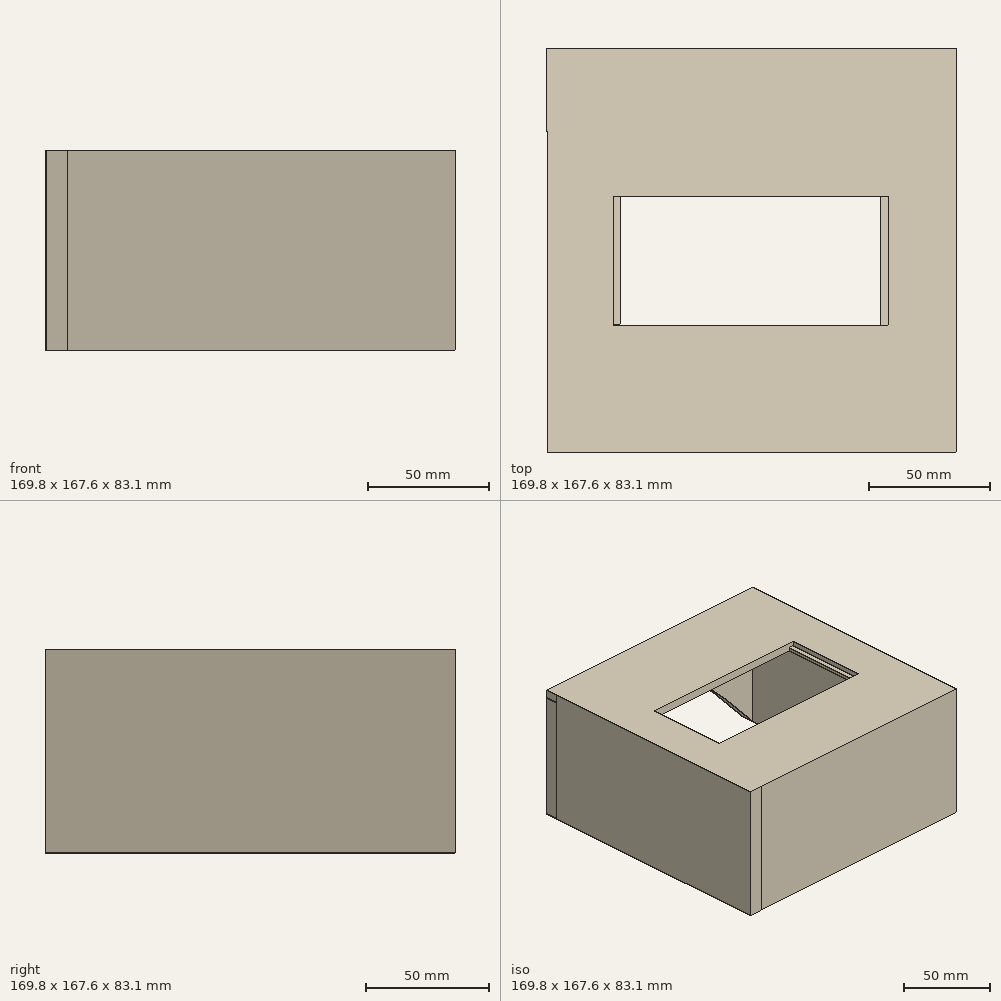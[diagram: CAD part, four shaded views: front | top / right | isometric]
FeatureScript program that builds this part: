
annotation { "Feature Type Name" : "Feature", "Feature Type Description" : "" }
export const myFeature = defineFeature(function(context is Context, id is Id, definition is map)
    precondition{}
    {
        {
            var Q0;
            Q0=qCreatedBy(makeId("Top.planeOp"),FACE);
            var sketch = newSketch(context, id + "F0", { "sketchPlane" : qUnion([Q0])});
            skLineSegment(sketch, "E0", {"start": v(-75.94, 0) * mm, "end": v(-75.94, -75.61) * mm});
            skLineSegment(sketch, "E1", {"start": v(-75.94, -75.61) * mm, "end": v(76.09, -75.61) * mm});
            skLineSegment(sketch, "E2", {"start": v(76.09, -75.61) * mm, "end": v(76.09, 75.88) * mm});
            skLineSegment(sketch, "E3", {"start": v(76.09, 75.88) * mm, "end": v(-76.12, 75.88) * mm});
            skLineSegment(sketch, "E4", {"start": v(-76.12, 75.88) * mm, "end": v(-75.94, -13.47) * mm});
            skLineSegment(sketch, "E5", {"start": v(-75.94, -13.47) * mm, "end": v(-57.32, -13.47) * mm});
            skLineSegment(sketch, "E6", {"start": v(-57.32, -13.47) * mm, "end": v(-57.32, 59.23) * mm});
            skLineSegment(sketch, "E7", {"start": v(-57.32, 59.23) * mm, "end": v(56.75, 59.23) * mm});
            skLineSegment(sketch, "E8", {"start": v(56.75, 59.23) * mm, "end": v(56.75, -58.96) * mm});
            skLineSegment(sketch, "E9", {"start": v(56.75, -58.96) * mm, "end": v(-57.32, -58.96) * mm});
            skLineSegment(sketch, "E10", {"start": v(-57.32, -58.96) * mm, "end": v(-57.32, -13.47) * mm});
            skSolve(sketch);
        }
        {
            var Q0;
            {var subQ0=sQuery(id+"F0.wireOp",EDGE,"E1");Q0=makeQuery(id+"F0.imprint","IMPRINT",FACE,{"disambiguationData":[TD([[makeQuery(id+"F0.imprint","IMPRINT",EDGE,{"derivedFrom":subQ0}),1.0]])]});}
            extrude(context, id + "F1", {"entities" : qUnion([Q0]), "depth" : 4.96 * mm});
        }
        {
            var Q0;
            Q0=makeQuery(id+"F1.opExtrude","SWEPT_FACE",FACE,{"disambiguationData":[OSD([sQuery(id+"F0.wireOp",EDGE,"E7")])]});
            extrude(context, id + "F2", {"entities" : qUnion([Q0]), "operationType" : NewBodyOperationType.ADD, "depth" : 36.28 * mm});
        }
        {
            var Q0;
            Q0=makeQuery(id+"F1.opExtrude","SWEPT_FACE",FACE,{"disambiguationData":[OSD([sQuery(id+"F0.wireOp",EDGE,"E9")])]});
            extrude(context, id + "F3", {"entities" : qUnion([Q0]), "operationType" : NewBodyOperationType.ADD, "depth" : 28.3 * mm});
        }
        {
            var Q0;
            Q0=makeQuery(id+"F1.opExtrude","SWEPT_FACE",FACE,{"disambiguationData":[OSD([sQuery(id+"F0.wireOp",EDGE,"E2")])]});
            var sketch = newSketch(context, id + "F4", { "sketchPlane" : qUnion([Q0])});
            skLineSegment(sketch, "E11.bottom", {"start": v(-75.61, 4.96) * mm, "end": v(75.88, 4.96) * mm});
            skLineSegment(sketch, "E11.top", {"start": v(-75.61, -78.08) * mm, "end": v(75.88, -78.08) * mm});
            skLineSegment(sketch, "E11.left", {"start": v(-75.61, 4.96) * mm, "end": v(-75.61, -78.08) * mm});
            skLineSegment(sketch, "E11.right", {"start": v(75.88, 4.96) * mm, "end": v(75.88, -78.08) * mm});
            skSolve(sketch);
        }
        {
            var Q0;
            Q0=makeQuery(id+"F1.opExtrude","SWEPT_FACE",FACE,{"disambiguationData":[OSD([sQuery(id+"F0.wireOp",EDGE,"E4")])]});
            var sketch = newSketch(context, id + "F5", { "sketchPlane" : qUnion([Q0])});
            skLineSegment(sketch, "E12.bottom", {"start": v(-76.03, 4.96) * mm, "end": v(75.62, 4.96) * mm});
            skLineSegment(sketch, "E12.top", {"start": v(-76.03, -78.18) * mm, "end": v(75.62, -78.18) * mm});
            skLineSegment(sketch, "E12.left", {"start": v(-76.03, 4.96) * mm, "end": v(-76.03, -78.18) * mm});
            skLineSegment(sketch, "E12.right", {"start": v(75.62, 4.96) * mm, "end": v(75.62, -78.18) * mm});
            skSolve(sketch);
        }
        {
            var Q0;
            Q0=makeQuery(id+"F1.opExtrude","SWEPT_FACE",FACE,{"disambiguationData":[OSD([sQuery(id+"F0.wireOp",EDGE,"E1")])]});
            var sketch = newSketch(context, id + "F6", { "sketchPlane" : qUnion([Q0])});
            skLineSegment(sketch, "E13.bottom", {"start": v(-75.94, 4.96) * mm, "end": v(76.09, 4.96) * mm});
            skLineSegment(sketch, "E13.top", {"start": v(-75.94, -77.97) * mm, "end": v(76.09, -77.97) * mm});
            skLineSegment(sketch, "E13.left", {"start": v(-75.94, 4.96) * mm, "end": v(-75.94, -77.97) * mm});
            skLineSegment(sketch, "E13.right", {"start": v(76.09, 4.96) * mm, "end": v(76.09, -77.97) * mm});
            skSolve(sketch);
        }
        {
            var Q0;
            {var subQ0=sQuery(id+"F6.wireOp",EDGE,"E13.top");Q0=makeQuery(id+"F6.imprint","IMPRINT",FACE,{"disambiguationData":[TD([[makeQuery(id+"F6.imprint","IMPRINT",EDGE,{"derivedFrom":subQ0}),1.0]])]});}
            var Q1;
            {var subQ0=sQuery(id+"F6.wireOp",EDGE,"E13.bottom");Q1=makeQuery(id+"F6.imprint","IMPRINT",FACE,{"disambiguationData":[TD([[makeQuery(id+"F6.imprint","IMPRINT",EDGE,{"derivedFrom":subQ0}),-1.0]])]});}
            extrude(context, id + "F7", {"entities" : qUnion([Q0, Q1]), "operationType" : NewBodyOperationType.ADD, "depth" : 7.7 * mm});
        }
        {
            var Q0;
            {var subQ3=sQuery(id+"F5.wireOp",EDGE,"E12.top");Q0=makeQuery(id+"F5.imprint","IMPRINT",FACE,{"disambiguationData":[TD([[makeQuery(id+"F5.imprint","IMPRINT",EDGE,{"derivedFrom":subQ3}),1.0]])]});}
            var Q1;
            {var subQ3=sQuery(id+"F0.wireOp",EDGE,"E4");var subQ5=makeQuery(id+"F1.opExtrude","CAP_EDGE",EDGE,{"disambiguationData":[OSD([subQ3])],"isStart":true});Q1=makeQuery(id+"F5.imprint","IMPRINT",FACE,{"disambiguationData":[TD([[makeQuery(id+"F5.imprint","IMPRINT",EDGE,{"derivedFrom":subQ5}),1.0]])]});}
            extrude(context, id + "F8", {"entities" : qUnion([Q0, Q1]), "operationType" : NewBodyOperationType.ADD, "depth" : 8.64 * mm});
        }
        {
            var Q0;
            {var subQ0=sQuery(id+"F4.wireOp",EDGE,"E11.top");Q0=makeQuery(id+"F4.imprint","IMPRINT",FACE,{"disambiguationData":[TD([[makeQuery(id+"F4.imprint","IMPRINT",EDGE,{"derivedFrom":subQ0}),1.0]])]});}
            var Q1;
            {var subQ0=sQuery(id+"F4.wireOp",EDGE,"E11.bottom");Q1=makeQuery(id+"F4.imprint","IMPRINT",FACE,{"disambiguationData":[TD([[makeQuery(id+"F4.imprint","IMPRINT",EDGE,{"derivedFrom":subQ0}),-1.0]])]});}
            var Q2;
            Q2=makeQuery(id+"F7.boolean.opBoolean","MERGE",FACE,{"derivedFrom":[makeQuery(id+"F1.opExtrude","SWEPT_FACE",FACE,{"disambiguationData":[OSD([sQuery(id+"F0.wireOp",EDGE,"E2")])]}),makeQuery(id+"F7.opExtrude","SWEPT_FACE",FACE,{"disambiguationData":[OSD([sQuery(id+"F6.wireOp",EDGE,"E13.right")])]})]});
            extrude(context, id + "F9", {"entities" : qUnion([Q0, Q1, Q2]), "operationType" : NewBodyOperationType.ADD, "depth" : 8.77 * mm});
        }
        {
            var Q0;
            Q0=makeQuery(id+"F7.boolean.opBoolean","MERGE",FACE,{"derivedFrom":[makeQuery(id+"F1.opExtrude","SWEPT_FACE",FACE,{"disambiguationData":[OSD([sQuery(id+"F0.wireOp",EDGE,"E0")])]}),makeQuery(id+"F7.opExtrude","SWEPT_FACE",FACE,{"disambiguationData":[OSD([sQuery(id+"F6.wireOp",EDGE,"E13.left")])]})]});
            var sketch = newSketch(context, id + "F10", { "sketchPlane" : qUnion([Q0])});
            skSolve(sketch);
        }
        {
            var Q0;
            Q0 = qSketchRegion(id + "F10", true);
            var Q1;
            Q1=makeQuery(id+"F8.opExtrude","SWEPT_FACE",FACE,{"disambiguationData":[OSD([sQuery(id+"F5.wireOp",EDGE,"E12.right")])]});
            extrude(context, id + "F11", {"entities" : qUnion([Q0, Q1]), "operationType" : NewBodyOperationType.ADD, "depth" : 7.64 * mm});
        }
        {
            var Q0;
            Q0=makeQuery(id+"F9.boolean.opBoolean","MERGE",FACE,{"derivedFrom":[makeQuery(id+"F1.opExtrude","SWEPT_FACE",FACE,{"disambiguationData":[OSD([sQuery(id+"F0.wireOp",EDGE,"E3")])]}),makeQuery(id+"F9.opExtrude","SWEPT_FACE",FACE,{"disambiguationData":[OSD([sQuery(id+"F4.wireOp",EDGE,"E11.right")])]})]});
            var sketch = newSketch(context, id + "F12", { "sketchPlane" : qUnion([Q0])});
            skFitSpline(sketch, "E14", {"points": [v(-76.09, -78.08) * mm, v(0, -14.04) * mm, v(76.51, -78.08) * mm], "startDerivative": vector(152.15, 192.16) * mm, "endDerivative": vector(153.05, -192.05) * mm});
            skSolve(sketch);
        }
        {
            var Q0;
            {var subQ1=sQuery(id+"F0.wireOp",EDGE,"E3");Q0=makeQuery(id+"F12.imprint","IMPRINT",FACE,{"disambiguationData":[TD([[makeQuery(id+"F12.imprint","IMPRINT",EDGE,{"derivedFrom":makeQuery(id+"F1.opExtrude","CAP_EDGE",EDGE,{"disambiguationData":[OSD([subQ1])],"isStart":true})}),1.0]])]});}
            var sketch = newSketch(context, id + "F13", { "sketchPlane" : qUnion([Q0])});
            skLineSegment(sketch, "E15", {"start": v(0, 0) * mm, "end": v(84.92, 0) * mm});
            skLineSegment(sketch, "E16", {"start": v(84.92, 0) * mm, "end": v(84.92, -77.55) * mm});
            skLineSegment(sketch, "E17", {"start": v(84.92, -77.55) * mm, "end": v(76.3, -77.55) * mm});
            skLineSegment(sketch, "E18", {"start": v(76.3, -77.55) * mm, "end": v(76.3, -14.05) * mm});
            skLineSegment(sketch, "E19", {"start": v(76.3, -14.05) * mm, "end": v(-76.33, -14.05) * mm});
            skLineSegment(sketch, "E20", {"start": v(-76.33, -14.05) * mm, "end": v(-76.33, -77.57) * mm});
            skLineSegment(sketch, "E21", {"start": v(-76.33, -77.57) * mm, "end": v(-85.18, -77.57) * mm});
            skLineSegment(sketch, "E22", {"start": v(-85.18, -77.57) * mm, "end": v(-85.18, 0) * mm});
            skLineSegment(sketch, "E23", {"start": v(-85.18, 0) * mm, "end": v(0, 0) * mm});
            skSolve(sketch);
        }
        {
            var Q0;
            {var subQ1=sQuery(id+"F0.wireOp",EDGE,"E3");Q0=makeQuery(id+"F12.imprint","IMPRINT",FACE,{"disambiguationData":[TD([[makeQuery(id+"F12.imprint","IMPRINT",EDGE,{"derivedFrom":makeQuery(id+"F1.opExtrude","CAP_EDGE",EDGE,{"disambiguationData":[OSD([subQ1])],"isStart":true})}),1.0]])]});}
            var Q1;
            {var subQ0=sQuery(id+"F13.wireOp",EDGE,"E16");Q1=makeQuery(id+"F13.imprint","IMPRINT",FACE,{"disambiguationData":[TD([[makeQuery(id+"F13.imprint","IMPRINT",EDGE,{"derivedFrom":subQ0}),-1.0]])]});}
            var Q2;
            Q2=makeQuery(id+"F8.opExtrude","SWEPT_FACE",FACE,{"disambiguationData":[OSD([sQuery(id+"F5.wireOp",EDGE,"E12.left")])]});
            extrude(context, id + "F14", {"entities" : qUnion([Q0, Q1, Q2]), "operationType" : NewBodyOperationType.ADD, "depth" : 8.32 * mm});
        }
        {
            var Q0;
            {var subQ0=sQuery(id+"F4.wireOp",EDGE,"E11.right");Q0=makeQuery(id+"F14.boolean.opBoolean","MERGE",FACE,{"derivedFrom":[makeQuery(id+"F14.opExtrude","CAP_FACE",FACE,{"disambiguationData":[OSD([sQuery(id+"F0.wireOp",EDGE,"E3"),sQuery(id+"F0.wireOp",EDGE,"E4"),sQuery(id+"F4.wireOp",EDGE,"E11.bottom"),sQuery(id+"F4.wireOp",EDGE,"E11.top"),subQ0,sQuery(id+"F5.wireOp",EDGE,"E12.left")])],"isStart":false}),makeQuery(id+"F14.opExtrude","CAP_FACE",FACE,{"disambiguationData":[OSD([subQ0,sQuery(id+"F13.wireOp",EDGE,"E15"),sQuery(id+"F13.wireOp",EDGE,"E16"),sQuery(id+"F13.wireOp",EDGE,"E17"),sQuery(id+"F13.wireOp",EDGE,"E18"),sQuery(id+"F13.wireOp",EDGE,"E19"),sQuery(id+"F13.wireOp",EDGE,"E23")])],"isStart":false})]});}
            var sketch = newSketch(context, id + "F15", { "sketchPlane" : qUnion([Q0])});
            skPoint(sketch, "E24.1.internal.snap0", {"position": v(0.02, -14.05) * mm});
            skFitSpline(sketch, "E24", {"points": [v(-76.09, -78.08) * mm, v(0.02, -21.7) * mm, v(76.3, -77.55) * mm], "startDerivative": vector(152.02, 168.87) * mm, "endDerivative": vector(152.74, -167.86) * mm});
            skSolve(sketch);
        }
        {
            var Q0;
            Q0=makeQuery(id+"F15.imprint","IMPRINT",FACE,{"disambiguationData":[TD([[makeQuery(id+"F15.imprint","IMPRINT",EDGE,{"derivedFrom":sQuery(id+"F15.wireOp",EDGE,"E24")}),1.0]])]});
            extrude(context, id + "F16", {"entities" : qUnion([Q0]), "operationType" : NewBodyOperationType.ADD, "oppositeDirection" : true, "depth" : 8.66 * mm});
        }
        {
            var Q0;
            {var subQ0=sQuery(id+"F0.wireOp",EDGE,"E9");var subQ1=sQuery(id+"F0.wireOp",EDGE,"E7");Q0=makeQuery(id+"F3.boolean.opBoolean","MERGE",FACE,{"derivedFrom":[makeQuery(id+"F2.boolean.opBoolean","MERGE",FACE,{"derivedFrom":[makeQuery(id+"F1.opExtrude","CAP_FACE",FACE,{"disambiguationData":[OSD([sQuery(id+"F0.wireOp",EDGE,"E0"),sQuery(id+"F0.wireOp",EDGE,"E1"),sQuery(id+"F0.wireOp",EDGE,"E2"),sQuery(id+"F0.wireOp",EDGE,"E3"),sQuery(id+"F0.wireOp",EDGE,"E4"),sQuery(id+"F0.wireOp",EDGE,"E6"),subQ1,sQuery(id+"F0.wireOp",EDGE,"E8"),subQ0,sQuery(id+"F0.wireOp",EDGE,"E10")])],"isStart":true}),makeQuery(id+"F2.opExtrude","SWEPT_FACE",FACE,{"disambiguationData":[OSD([subQ1]),TDD([makeQuery(id+"F1.opExtrude","CAP_EDGE",EDGE,{"disambiguationData":[OSD([subQ1])],"isStart":true})])]})]}),makeQuery(id+"F3.opExtrude","SWEPT_FACE",FACE,{"disambiguationData":[OSD([subQ0]),TDD([makeQuery(id+"F1.opExtrude","CAP_EDGE",EDGE,{"disambiguationData":[OSD([subQ0])],"isStart":true})])]})]});}
            var sketch = newSketch(context, id + "F17", { "sketchPlane" : qUnion([Q0])});
            skLineSegment(sketch, "E25", {"start": v(56.75, -22.94) * mm, "end": v(53.38, -22.94) * mm});
            skLineSegment(sketch, "E26", {"start": v(53.38, -22.94) * mm, "end": v(53.38, 30.66) * mm});
            skLineSegment(sketch, "E27", {"start": v(53.38, 30.66) * mm, "end": v(56.75, 30.66) * mm});
            skLineSegment(sketch, "E28", {"start": v(56.75, 30.66) * mm, "end": v(56.75, -22.94) * mm});
            skSolve(sketch);
        }
        {
            var Q0;
            {var subQ7=sQuery(id+"F17.wireOp",EDGE,"E25");Q0=makeQuery(id+"F17.imprint","IMPRINT",FACE,{"disambiguationData":[TD([[makeQuery(id+"F17.imprint","IMPRINT",EDGE,{"derivedFrom":subQ7}),-1.0]])]});}
            var sketch = newSketch(context, id + "F18", { "sketchPlane" : qUnion([Q0])});
            skLineSegment(sketch, "E29", {"start": v(-57.09, 30.4) * mm, "end": v(-57.09, -22.82) * mm});
            skLineSegment(sketch, "E30", {"start": v(-57.09, -22.82) * mm, "end": v(-54.16, -22.82) * mm});
            skLineSegment(sketch, "E31", {"start": v(-54.16, -22.82) * mm, "end": v(-54.16, 30.4) * mm});
            skLineSegment(sketch, "E32", {"start": v(-54.16, 30.4) * mm, "end": v(-57.09, 30.4) * mm});
            skSolve(sketch);
        }
        {
            var Q0;
            Q0=makeQuery(id+"F18.imprint","IMPRINT",FACE,{"disambiguationData":[TD([[makeQuery(id+"F18.imprint","IMPRINT",EDGE,{"derivedFrom":sQuery(id+"F18.wireOp",EDGE,"E29")}),1.0]])]});
            var Q1;
            Q1=makeQuery(id+"F17.imprint","IMPRINT",FACE,{"disambiguationData":[TD([[makeQuery(id+"F17.imprint","IMPRINT",EDGE,{"derivedFrom":sQuery(id+"F17.wireOp",EDGE,"E25")}),1.0]])]});
            extrude(context, id + "F19", {"entities" : qUnion([Q0, Q1]), "operationType" : NewBodyOperationType.ADD, "oppositeDirection" : true, "depth" : 2.05 * mm});
        }
    });
